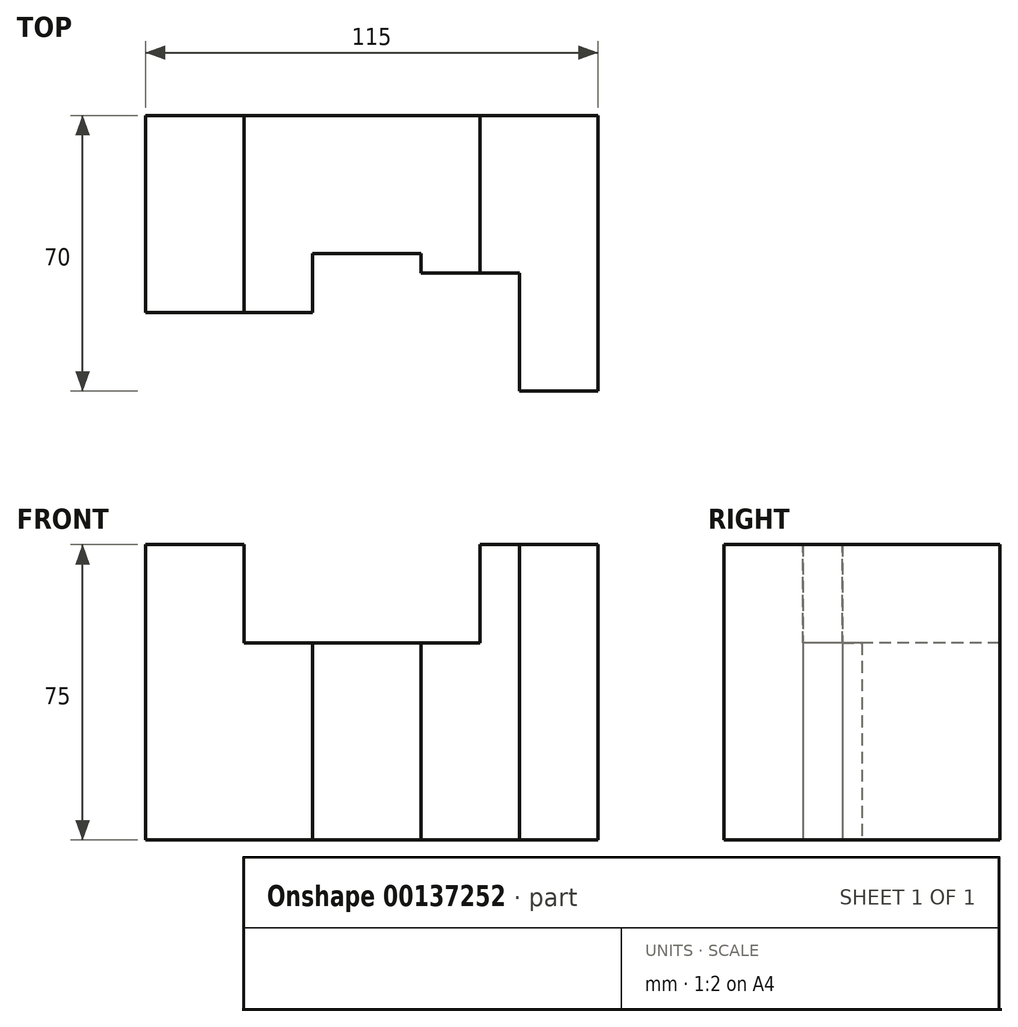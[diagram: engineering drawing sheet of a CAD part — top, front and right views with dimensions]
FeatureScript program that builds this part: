
annotation { "Feature Type Name" : "Feature", "Feature Type Description" : "" }
export const myFeature = defineFeature(function(context is Context, id is Id, definition is map)
    precondition{}
    {
        {
            var Q0;
            Q0=qCreatedBy(makeId("Top.planeOp"),FACE);
            var sketch = newSketch(context, id + "F0", { "sketchPlane" : qUnion([Q0])});
            skLineSegment(sketch, "E0", {"start": v(0, 0) * mm, "end": v(0, 50) * mm});
            skLineSegment(sketch, "E1", {"start": v(0, 50) * mm, "end": v(115, 50) * mm});
            skLineSegment(sketch, "E2", {"start": v(115, 50) * mm, "end": v(115, -20) * mm});
            skLineSegment(sketch, "E3", {"start": v(115, -20) * mm, "end": v(95, -20) * mm});
            skLineSegment(sketch, "E4", {"start": v(95, -20) * mm, "end": v(95, 10) * mm});
            skLineSegment(sketch, "E5", {"start": v(95, 10) * mm, "end": v(70, 10) * mm});
            skLineSegment(sketch, "E6", {"start": v(70, 10) * mm, "end": v(70, 15) * mm});
            skLineSegment(sketch, "E7", {"start": v(70, 15) * mm, "end": v(42.5, 15) * mm});
            skLineSegment(sketch, "E8", {"start": v(42.5, 15) * mm, "end": v(42.5, 0) * mm});
            skLineSegment(sketch, "E9", {"start": v(42.5, 0) * mm, "end": v(0, 0) * mm});
            skSolve(sketch);
        }
        {
            var Q0;
            Q0 = qSketchRegion(id + "F0", true);
            extrude(context, id + "F1", {"entities" : qUnion([Q0]), "depth" : 75 * mm});
        }
        {
            var Q0;
            Q0=makeQuery(id+"F1.opExtrude","CAP_FACE",FACE,{"disambiguationData":[OSD([sQuery(id+"F0.wireOp",EDGE,"E0"),sQuery(id+"F0.wireOp",EDGE,"E1"),sQuery(id+"F0.wireOp",EDGE,"E2"),sQuery(id+"F0.wireOp",EDGE,"E3"),sQuery(id+"F0.wireOp",EDGE,"E4"),sQuery(id+"F0.wireOp",EDGE,"E5"),sQuery(id+"F0.wireOp",EDGE,"E6"),sQuery(id+"F0.wireOp",EDGE,"E7"),sQuery(id+"F0.wireOp",EDGE,"E8"),sQuery(id+"F0.wireOp",EDGE,"E9")])],"isStart":false});
            var sketch = newSketch(context, id + "F2", { "sketchPlane" : qUnion([Q0])});
            skLineSegment(sketch, "E10", {"start": v(25, 50) * mm, "end": v(25, 0) * mm});
            skLineSegment(sketch, "E11", {"start": v(25, 50) * mm, "end": v(85, 50) * mm});
            skLineSegment(sketch, "E12", {"start": v(85, 50) * mm, "end": v(85, 10) * mm});
            skLineSegment(sketch, "E13", {"start": v(85, 10) * mm, "end": v(95, 10) * mm});
            skLineSegment(sketch, "E14", {"start": v(95, 10) * mm, "end": v(95, 0) * mm});
            skLineSegment(sketch, "E15", {"start": v(95, 0) * mm, "end": v(25, 0) * mm});
            skSolve(sketch);
        }
        {
            var Q0;
            {var subQ2=sQuery(id+"F2.wireOp",EDGE,"E10");Q0=makeQuery(id+"F2.imprint","IMPRINT",FACE,{"disambiguationData":[TD([[makeQuery(id+"F2.imprint","IMPRINT",EDGE,{"derivedFrom":subQ2}),1.0]])]});}
            extrude(context, id + "F3", {"entities" : qUnion([Q0]), "operationType" : NewBodyOperationType.REMOVE, "oppositeDirection" : true, "depth" : 25 * mm});
        }
    });
